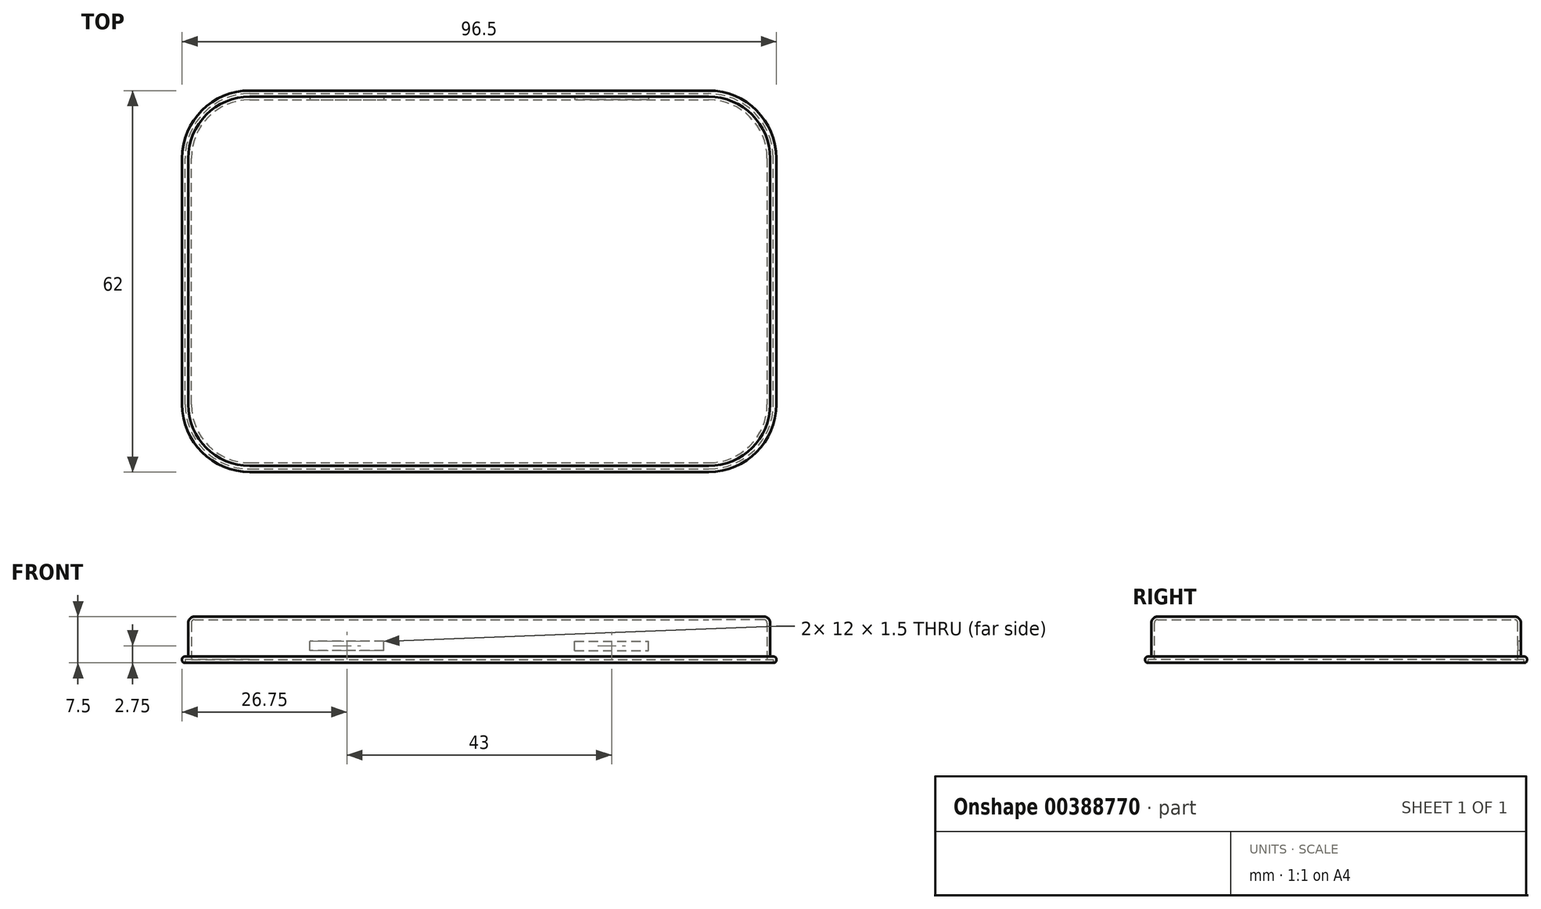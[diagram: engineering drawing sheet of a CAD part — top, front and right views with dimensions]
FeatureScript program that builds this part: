
annotation { "Feature Type Name" : "Feature", "Feature Type Description" : "" }
export const myFeature = defineFeature(function(context is Context, id is Id, definition is map)
    precondition{}
    {
        {
            var Q0;
            Q0=qCreatedBy(makeId("Top.planeOp"),FACE);
            var sketch = newSketch(context, id + "F0", { "sketchPlane" : qUnion([Q0])});
            skLineSegment(sketch, "E0.bottom", {"start": v(-37.25, 30) * mm, "end": v(37.25, 30) * mm});
            skLineSegment(sketch, "E0.top", {"start": v(-37.25, -30) * mm, "end": v(37.25, -30) * mm});
            skLineSegment(sketch, "E0.left", {"start": v(-47.25, 20) * mm, "end": v(-47.25, -20) * mm});
            skLineSegment(sketch, "E0.right", {"start": v(47.25, 20) * mm, "end": v(47.25, -20) * mm});
            skPoint(sketch, "E0.middle", {"position": v(0, 0) * mm});
            skPoint(sketch, "E1.visualSharp", {"position": v(-47.25, 30) * mm});
            skArc(sketch, "E1.filletArc", {"start": v(-37.25, 30) * mm, "mid": v(-44.32, 27.07) * mm, "end": v(-47.25, 20) * mm});
            skPoint(sketch, "E2.visualSharp", {"position": v(-47.25, -30) * mm});
            skArc(sketch, "E2.filletArc", {"start": v(-47.25, -20) * mm, "mid": v(-44.32, -27.07) * mm, "end": v(-37.25, -30) * mm});
            skPoint(sketch, "E3.visualSharp", {"position": v(47.25, -30) * mm});
            skArc(sketch, "E3.filletArc", {"start": v(37.25, -30) * mm, "mid": v(44.32, -27.07) * mm, "end": v(47.25, -20) * mm});
            skPoint(sketch, "E4.visualSharp", {"position": v(47.25, 30) * mm});
            skArc(sketch, "E4.filletArc", {"start": v(47.25, 20) * mm, "mid": v(44.32, 27.07) * mm, "end": v(37.25, 30) * mm});
            skSolve(sketch);
        }
        {
            var Q0;
            Q0 = qSketchRegion(id + "F0", true);
            extrude(context, id + "F1", {"entities" : qUnion([Q0]), "depth" : 7.5 * mm});
        }
        {
            var Q0;
            Q0=makeQuery(id+"F1.opExtrude","CAP_EDGE",EDGE,{"disambiguationData":[OSD([sQuery(id+"F0.wireOp",EDGE,"E0.left")])],"isStart":false});
            var Q1;
            Q1=makeQuery(id+"F1.opExtrude","CAP_EDGE",EDGE,{"disambiguationData":[OSD([sQuery(id+"F0.wireOp",EDGE,"E0.top")])],"isStart":false});
            var Q2;
            Q2=makeQuery(id+"F1.opExtrude","CAP_EDGE",EDGE,{"disambiguationData":[OSD([sQuery(id+"F0.wireOp",EDGE,"E2.filletArc")])],"isStart":false});
            var Q3;
            Q3=makeQuery(id+"F1.opExtrude","CAP_EDGE",EDGE,{"disambiguationData":[OSD([sQuery(id+"F0.wireOp",EDGE,"E3.filletArc")])],"isStart":false});
            var Q4;
            Q4=makeQuery(id+"F1.opExtrude","CAP_EDGE",EDGE,{"disambiguationData":[OSD([sQuery(id+"F0.wireOp",EDGE,"E0.right")])],"isStart":false});
            var Q5;
            Q5=makeQuery(id+"F1.opExtrude","CAP_EDGE",EDGE,{"disambiguationData":[OSD([sQuery(id+"F0.wireOp",EDGE,"E4.filletArc")])],"isStart":false});
            var Q6;
            Q6=makeQuery(id+"F1.opExtrude","CAP_EDGE",EDGE,{"disambiguationData":[OSD([sQuery(id+"F0.wireOp",EDGE,"E0.bottom")])],"isStart":false});
            var Q7;
            Q7=makeQuery(id+"F1.opExtrude","CAP_EDGE",EDGE,{"disambiguationData":[OSD([sQuery(id+"F0.wireOp",EDGE,"E1.filletArc")])],"isStart":false});
            fillet(context, id + "F2", {"entities" : qUnion([Q0, Q1, Q2, Q3, Q4, Q5, Q6, Q7]), "radius" : 1 * mm, "tangentPropagation" : true, "allowEdgeOverflow" : false});
        }
        {
            var Q0;
            Q0=qCreatedBy(makeId("Top.planeOp"),FACE);
            var sketch = newSketch(context, id + "F3", { "sketchPlane" : qUnion([Q0])});
            skLineSegment(sketch, "E5.0", {"start": v(-37.25, 31) * mm, "end": v(37.25, 31) * mm});
            skArc(sketch, "E5.1", {"start": v(48.25, 20) * mm, "mid": v(45.03, 27.78) * mm, "end": v(37.25, 31) * mm});
            skArc(sketch, "E5.2", {"start": v(-37.25, 31) * mm, "mid": v(-45.03, 27.78) * mm, "end": v(-48.25, 20) * mm});
            skLineSegment(sketch, "E5.3", {"start": v(48.25, 20) * mm, "end": v(48.25, -20) * mm});
            skLineSegment(sketch, "E5.4", {"start": v(-48.25, 20) * mm, "end": v(-48.25, -20) * mm});
            skArc(sketch, "E5.5", {"start": v(-48.25, -20) * mm, "mid": v(-45.03, -27.78) * mm, "end": v(-37.25, -31) * mm});
            skLineSegment(sketch, "E5.6", {"start": v(-37.25, -31) * mm, "end": v(37.25, -31) * mm});
            skArc(sketch, "E5.7", {"start": v(37.25, -31) * mm, "mid": v(45.03, -27.78) * mm, "end": v(48.25, -20) * mm});
            skSolve(sketch);
        }
        {
            var Q0;
            Q0 = qSketchRegion(id + "F3", true);
            extrude(context, id + "F4", {"entities" : qUnion([Q0]), "operationType" : NewBodyOperationType.ADD, "depth" : 1 * mm});
        }
        {
            var Q0;
            Q0=makeQuery(id+"F4.opExtrude","CAP_EDGE",EDGE,{"disambiguationData":[OSD([sQuery(id+"F3.wireOp",EDGE,"E5.4")])],"isStart":false});
            var Q1;
            Q1=makeQuery(id+"F4.opExtrude","CAP_EDGE",EDGE,{"disambiguationData":[OSD([sQuery(id+"F3.wireOp",EDGE,"E5.5")])],"isStart":false});
            var Q2;
            Q2=makeQuery(id+"F4.opExtrude","CAP_EDGE",EDGE,{"disambiguationData":[OSD([sQuery(id+"F3.wireOp",EDGE,"E5.6")])],"isStart":false});
            var Q3;
            Q3=makeQuery(id+"F4.opExtrude","CAP_EDGE",EDGE,{"disambiguationData":[OSD([sQuery(id+"F3.wireOp",EDGE,"E5.6")])],"isStart":true});
            var Q4;
            Q4=makeQuery(id+"F4.opExtrude","CAP_EDGE",EDGE,{"disambiguationData":[OSD([sQuery(id+"F3.wireOp",EDGE,"E5.5")])],"isStart":true});
            var Q5;
            Q5=makeQuery(id+"F4.opExtrude","CAP_EDGE",EDGE,{"disambiguationData":[OSD([sQuery(id+"F3.wireOp",EDGE,"E5.4")])],"isStart":true});
            var Q6;
            Q6=makeQuery(id+"F4.opExtrude","CAP_EDGE",EDGE,{"disambiguationData":[OSD([sQuery(id+"F3.wireOp",EDGE,"E5.7")])],"isStart":false});
            var Q7;
            Q7=makeQuery(id+"F4.opExtrude","CAP_EDGE",EDGE,{"disambiguationData":[OSD([sQuery(id+"F3.wireOp",EDGE,"E5.7")])],"isStart":true});
            var Q8;
            Q8=makeQuery(id+"F4.opExtrude","CAP_EDGE",EDGE,{"disambiguationData":[OSD([sQuery(id+"F3.wireOp",EDGE,"E5.3")])],"isStart":false});
            var Q9;
            Q9=makeQuery(id+"F4.opExtrude","CAP_EDGE",EDGE,{"disambiguationData":[OSD([sQuery(id+"F3.wireOp",EDGE,"E5.3")])],"isStart":true});
            var Q10;
            Q10=makeQuery(id+"F4.opExtrude","CAP_EDGE",EDGE,{"disambiguationData":[OSD([sQuery(id+"F3.wireOp",EDGE,"E5.1")])],"isStart":false});
            var Q11;
            Q11=makeQuery(id+"F4.opExtrude","CAP_EDGE",EDGE,{"disambiguationData":[OSD([sQuery(id+"F3.wireOp",EDGE,"E5.1")])],"isStart":true});
            var Q12;
            Q12=makeQuery(id+"F4.opExtrude","CAP_EDGE",EDGE,{"disambiguationData":[OSD([sQuery(id+"F3.wireOp",EDGE,"E5.0")])],"isStart":false});
            var Q13;
            Q13=makeQuery(id+"F4.opExtrude","CAP_EDGE",EDGE,{"disambiguationData":[OSD([sQuery(id+"F3.wireOp",EDGE,"E5.0")])],"isStart":true});
            var Q14;
            Q14=makeQuery(id+"F4.opExtrude","CAP_EDGE",EDGE,{"disambiguationData":[OSD([sQuery(id+"F3.wireOp",EDGE,"E5.2")])],"isStart":true});
            var Q15;
            Q15=makeQuery(id+"F4.opExtrude","CAP_EDGE",EDGE,{"disambiguationData":[OSD([sQuery(id+"F3.wireOp",EDGE,"E5.2")])],"isStart":false});
            fillet(context, id + "F5", {"entities" : qUnion([Q0, Q1, Q2, Q3, Q4, Q5, Q6, Q7, Q8, Q9, Q10, Q11, Q12, Q13, Q14, Q15]), "radius" : 0.4 * mm, "tangentPropagation" : true, "allowEdgeOverflow" : false});
        }
        {
            var Q0;
            Q0=makeQuery(id+"F4.boolean.opBoolean","MERGE",FACE,{"derivedFrom":[makeQuery(id+"F1.opExtrude","CAP_FACE",FACE,{"disambiguationData":[OSD([sQuery(id+"F0.wireOp",EDGE,"E0.bottom"),sQuery(id+"F0.wireOp",EDGE,"E0.top"),sQuery(id+"F0.wireOp",EDGE,"E0.left"),sQuery(id+"F0.wireOp",EDGE,"E0.right"),sQuery(id+"F0.wireOp",EDGE,"E1.filletArc"),sQuery(id+"F0.wireOp",EDGE,"E2.filletArc"),sQuery(id+"F0.wireOp",EDGE,"E3.filletArc"),sQuery(id+"F0.wireOp",EDGE,"E4.filletArc")])],"isStart":true}),makeQuery(id+"F4.opExtrude","CAP_FACE",FACE,{"disambiguationData":[OSD([sQuery(id+"F3.wireOp",EDGE,"E5.0"),sQuery(id+"F3.wireOp",EDGE,"E5.1"),sQuery(id+"F3.wireOp",EDGE,"E5.2"),sQuery(id+"F3.wireOp",EDGE,"E5.3"),sQuery(id+"F3.wireOp",EDGE,"E5.4"),sQuery(id+"F3.wireOp",EDGE,"E5.5"),sQuery(id+"F3.wireOp",EDGE,"E5.6"),sQuery(id+"F3.wireOp",EDGE,"E5.7")])],"isStart":true})]});
            shell(context, id + "F6", {"entities" : qUnion([Q0]), "thickness" : 0.5 * mm});
        }
        {
            var Q0;
            Q0=qCreatedBy(makeId("Front.planeOp"),FACE);
            var sketch = newSketch(context, id + "F7", { "sketchPlane" : qUnion([Q0])});
            skLineSegment(sketch, "E6.bottom", {"start": v(-15.5, 2) * mm, "end": v(-27.5, 2) * mm});
            skLineSegment(sketch, "E6.top", {"start": v(-15.5, 3.5) * mm, "end": v(-27.5, 3.5) * mm});
            skLineSegment(sketch, "E6.left", {"start": v(-15.5, 2) * mm, "end": v(-15.5, 3.5) * mm});
            skLineSegment(sketch, "E6.right", {"start": v(-27.5, 2) * mm, "end": v(-27.5, 3.5) * mm});
            skLineSegment(sketch, "E7", {"start": v(0, 74.73) * mm, "end": v(0, -41.37) * mm, "construction": true});
            skLineSegment(sketch, "E8.MirrorCS", {"start": v(27.5, 2) * mm, "end": v(27.5, 3.5) * mm});
            skLineSegment(sketch, "E9.MirrorCS", {"start": v(15.5, 2) * mm, "end": v(15.5, 3.5) * mm});
            skLineSegment(sketch, "E10.MirrorCS", {"start": v(15.5, 2) * mm, "end": v(27.5, 2) * mm});
            skLineSegment(sketch, "E11.MirrorCS", {"start": v(15.5, 3.5) * mm, "end": v(27.5, 3.5) * mm});
            skSolve(sketch);
        }
        {
            var Q0;
            Q0 = qSketchRegion(id + "F7", true);
            var Q1;
            Q1=makeQuery(id+"F1.opExtrude","SWEPT_FACE",FACE,{"disambiguationData":[OSD([sQuery(id+"F0.wireOp",EDGE,"E0.bottom")])]});
            extrude(context, id + "F8", {"entities" : qUnion([Q0]), "operationType" : NewBodyOperationType.REMOVE, "endBound" : BoundingType.UP_TO_SURFACE, "oppositeDirection" : true, "endBoundEntityFace" : qUnion([Q1]), "depth" : 50 * mm});
        }
    });
